# Revit family: Sanitary_Bidets_Sanindusa_Look_Wall-mounted-Bidet-With-Concealed-Fixation
name_source: partatom
category: Plumbing Fixtures
revit_build: Autodesk Revit 2018 (Build: 20170223_1515(x64)
units: mm (PartAtom-declared; Revit-internal decimal feet)

## family parameters
Cut with Voids When Loaded = No
Host = Face
Part Type = Normal
Room Calculation Point = No
Round Connector Dimension = Use Diameter
Shared = No

## types (1)
- Sanitary_Bidets_Sanindusa_Look_Wall-mounted-Bidet-With-Concealed-Fixation
    AssetType = Fixed
    BIMObjectName = Bidet_Look
    BidetMounting = wallhung
    Category = Pr_40_20_06_11,Bidets
    CodePerformance = EN 14528:2007 - CL 25
    Color = White
    Constituents = Compatible suport frames (not inluded): 439-Metal support for wall mounted bidet for pladur, 430-Metal support for wall mounted bidet. 48011-chromed embellishment ring (included)
    Default Elevation = 1219 mm
    Description = Waste water appliance for washing the excretory organs while sitting astride the bowl (BS6100)
    DrainSize = 46 mm  [stored 0.150919 ft]
    Element Type = BIDET: Waste water appliance for washing the excretory organs while sitting astride the bowl (BS6100)
    Features = Wall mounted bidet with concealed fixation, easy to clean and to install. For domestic and hotel use.
    Finish = Gloss
    Installation Instructions = https://www.tec.sanindusa.pt
    InstallationDate = 1900-12-31T23:59:59
    Manufacturer = Sanindusa
    ManufacturerName = Sanindusa
    ManufacturerURL = http://www.sanindusa.pt
    Material = Vitreous China
    Model = 134440004
    ModelNumber = 134440004
    ModelReference = Look
    Name = Bidet Look
    NominalHeight = 305 mm  [stored 1.00066 ft]
    NominalLength = 348 mm  [stored 1.14173 ft]
    NominalWidth = 385 mm  [stored 1.26312 ft]
    Pre-defined type (IFC) = BIDET
    ProductInformation = https://www.tec.sanindusa.pt
    ProductionYear = 2019
    Size = 348x385x305
    SpilloverLevel = 113
    Type (IFC) = IfcSanitaryTerminalType
    URL = www.tec.sanindusa.pt
    Uniclass2015Code = Pr_40_20_06_11
    Uniclass2015Title = Bidets
    Uniclass2015Version = Products v1.6
    Version = 1
    WarrantyDescription = https://www.tec.sanindusa.pt
    WarrantyDurationParts = 5
    WarrantyDurationUnit = year
    WarrantyStartDate = 1900-12-31T23:59:59
    Waste Connection = Yes
    Weight = 20.15 kg

note: [stored X ft] marks values corroborated as IEEE doubles in the binary element streams (Revit-internal decimal feet)

## geometry (parser evidence)
native form markers: Sweep x5
no freeform markers — native parametric forms only
